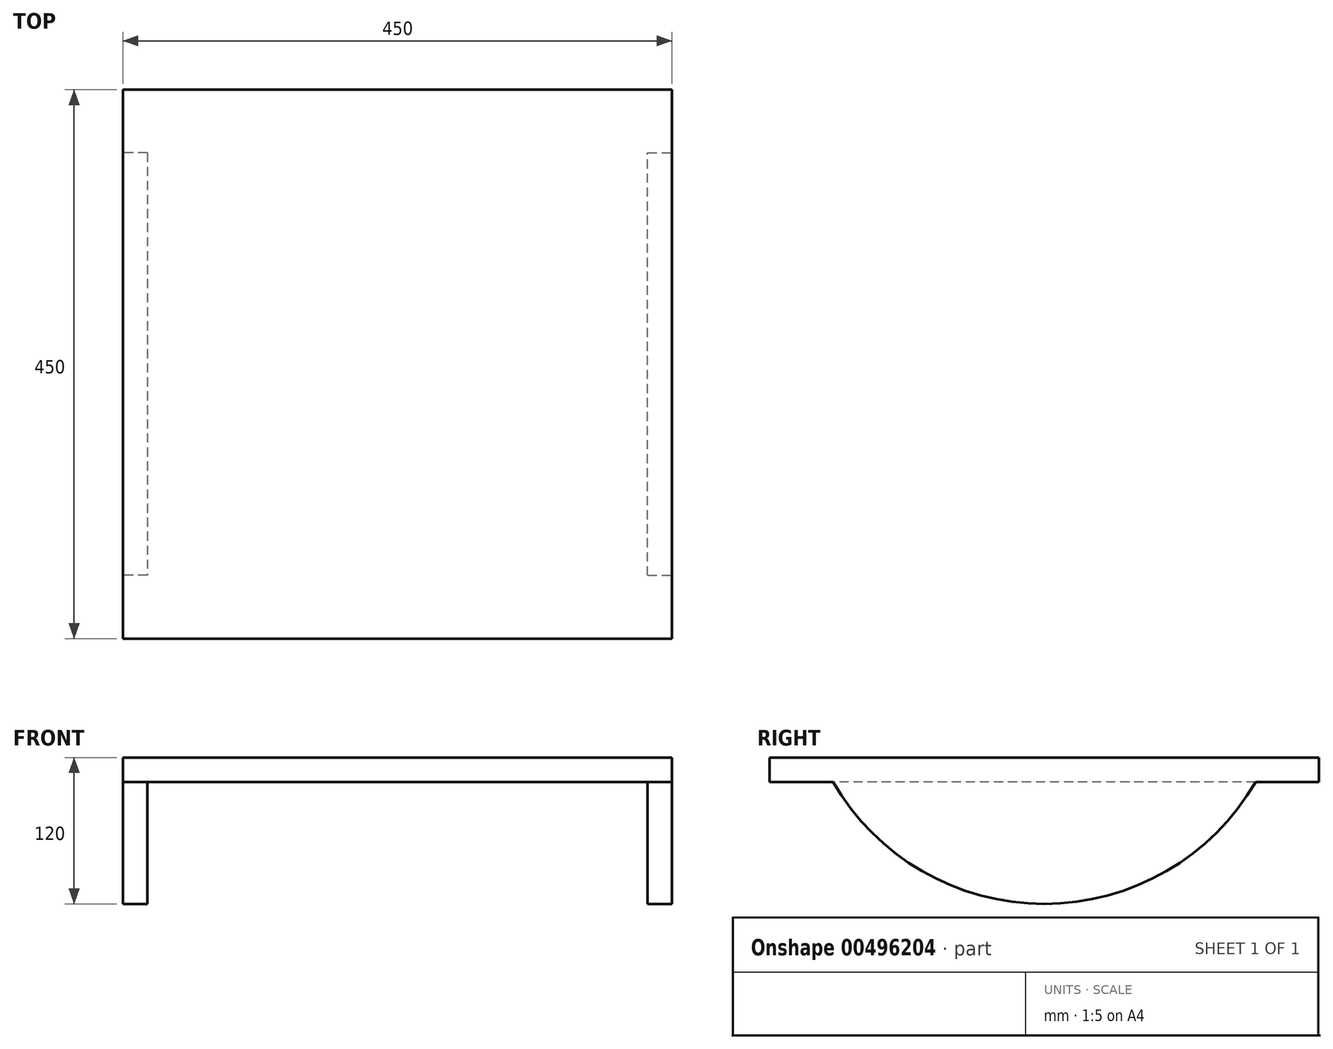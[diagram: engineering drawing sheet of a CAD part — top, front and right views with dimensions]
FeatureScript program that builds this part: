
annotation { "Feature Type Name" : "Feature", "Feature Type Description" : "" }
export const myFeature = defineFeature(function(context is Context, id is Id, definition is map)
    precondition{}
    {
        {
            var Q0;
            Q0=qCreatedBy(makeId("Right.planeOp"),FACE);
            var sketch = newSketch(context, id + "F0", { "sketchPlane" : qUnion([Q0])});
            skArc(sketch, "E0", {"start": v(-173.2, -100) * mm, "mid": v(0, -200) * mm, "end": v(173.2, -100) * mm});
            skLineSegment(sketch, "E1", {"start": v(-173.2, -100) * mm, "end": v(173.2, -100) * mm});
            skSolve(sketch);
        }
        {
            var Q0;
            Q0=makeQuery(id+"F0.imprint","IMPRINT",FACE,{"disambiguationData":[TD([[makeQuery(id+"F0.imprint","IMPRINT",EDGE,{"derivedFrom":sQuery(id+"F0.wireOp",EDGE,"E0")}),1.0]])]});
            extrude(context, id + "F1", {"entities" : qUnion([Q0]), "oppositeDirection" : true, "depth" : 20 * mm});
        }
        {
            var Q0;
            Q0=makeQuery(id+"F1.opExtrude","SWEPT_FACE",FACE,{"disambiguationData":[OSD([sQuery(id+"F0.wireOp",EDGE,"E1")])]});
            var sketch = newSketch(context, id + "F2", { "sketchPlane" : qUnion([Q0])});
            skLineSegment(sketch, "E2.bottom", {"start": v(-450, 225) * mm, "end": v(0, 225) * mm});
            skLineSegment(sketch, "E2.top", {"start": v(-450, -225) * mm, "end": v(0, -225) * mm});
            skLineSegment(sketch, "E2.left", {"start": v(-450, 225) * mm, "end": v(-450, -225) * mm});
            skLineSegment(sketch, "E2.right", {"start": v(0, 225) * mm, "end": v(0, -225) * mm});
            skSolve(sketch);
        }
        {
            var Q0;
            Q0 = qSketchRegion(id + "F2", true);
            var Q1;
            {var subQ4=sQuery(id+"F2.wireOp",EDGE,"E2.bottom");Q1=makeQuery(id+"F2.imprint","IMPRINT",FACE,{"disambiguationData":[TD([[makeQuery(id+"F2.imprint","IMPRINT",EDGE,{"derivedFrom":subQ4}),-1.0]])]});}
            extrude(context, id + "F3", {"entities" : qUnion([Q0, Q1]), "operationType" : NewBodyOperationType.ADD, "depth" : 20 * mm});
        }
        {
            var Q0;
            Q0=makeQuery(id+"F3.opExtrude","SWEPT_FACE",FACE,{"disambiguationData":[OSD([sQuery(id+"F2.wireOp",EDGE,"E2.left")])]});
            var sketch = newSketch(context, id + "F4", { "sketchPlane" : qUnion([Q0])});
            skArc(sketch, "E3", {"start": v(-173.2, -100) * mm, "mid": v(0, -200) * mm, "end": v(173.2, -100) * mm});
            skLineSegment(sketch, "E4", {"start": v(-173.2, -100) * mm, "end": v(173.2, -100) * mm});
            skSolve(sketch);
        }
        {
            var Q0;
            Q0 = qSketchRegion(id + "F4", true);
            var Q1;
            Q1=makeQuery(id+"F4.imprint","IMPRINT",FACE,{"disambiguationData":[TD([[makeQuery(id+"F4.imprint","IMPRINT",EDGE,{"derivedFrom":sQuery(id+"F4.wireOp",EDGE,"E3")}),1.0]])]});
            extrude(context, id + "F5", {"entities" : qUnion([Q0, Q1]), "operationType" : NewBodyOperationType.ADD, "oppositeDirection" : true, "depth" : 20 * mm});
        }
    });
